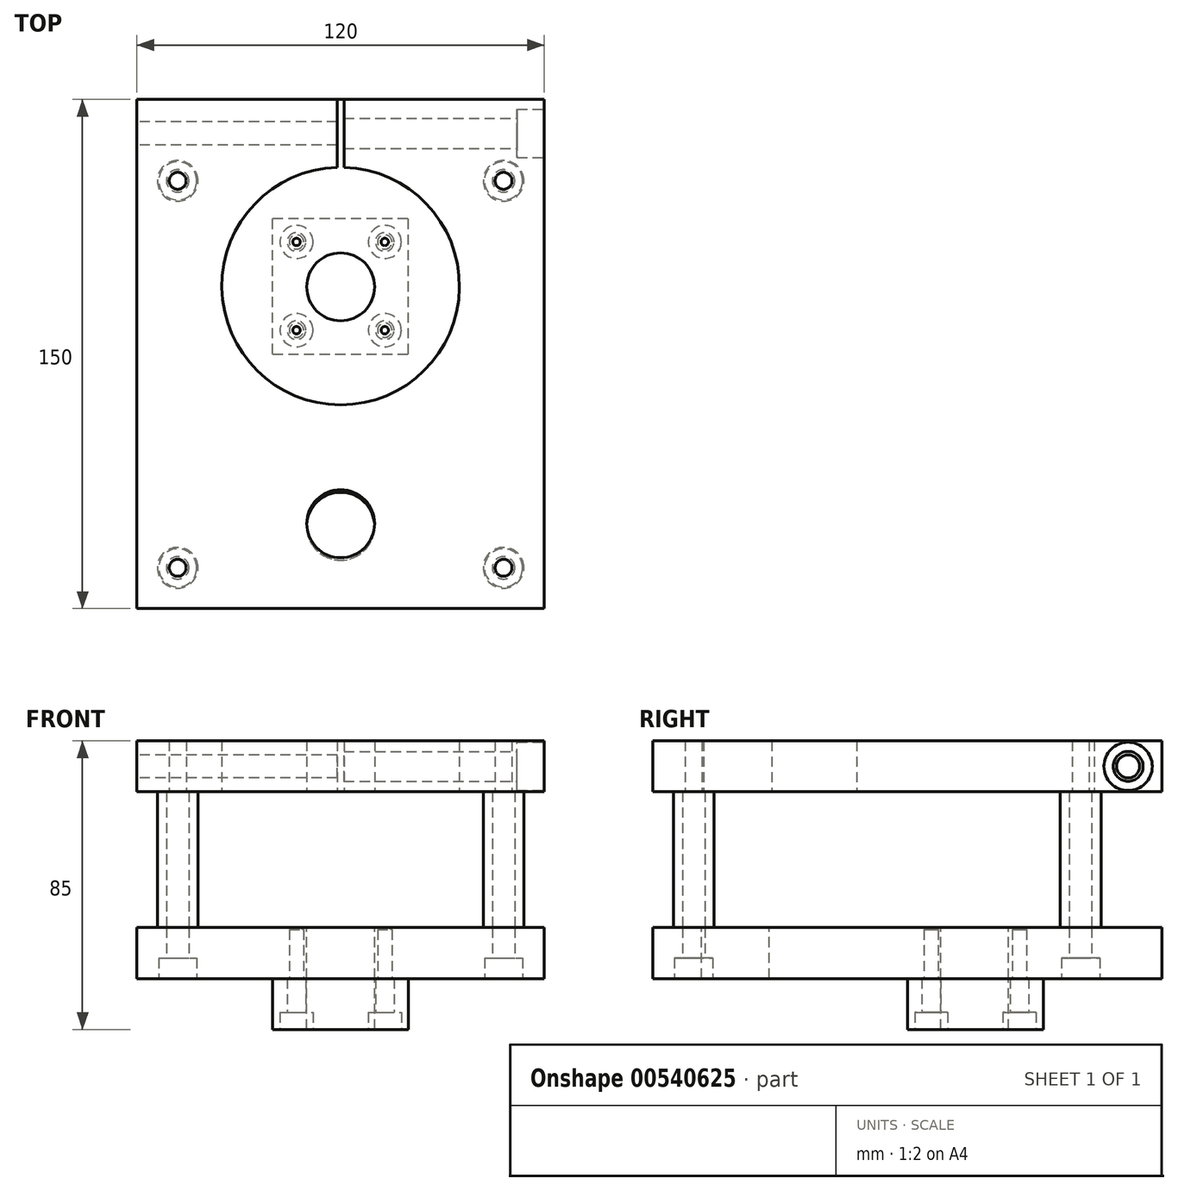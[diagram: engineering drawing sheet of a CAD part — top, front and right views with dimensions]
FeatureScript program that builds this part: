
annotation { "Feature Type Name" : "Feature", "Feature Type Description" : "" }
export const myFeature = defineFeature(function(context is Context, id is Id, definition is map)
    precondition{}
    {
        {
            var Q0;
            Q0=qCreatedBy(makeId("Top.planeOp"),FACE);
            var sketch = newSketch(context, id + "F0", { "sketchPlane" : qUnion([Q0])});
            skLineSegment(sketch, "E0.bottom", {"start": v(-60, 75) * mm, "end": v(-1, 75) * mm});
            skLineSegment(sketch, "E0.top", {"start": v(-60, -75) * mm, "end": v(60, -75) * mm});
            skLineSegment(sketch, "E0.left", {"start": v(-60, 75) * mm, "end": v(-60, -75) * mm});
            skLineSegment(sketch, "E0.right", {"start": v(60, 75) * mm, "end": v(60, -75) * mm});
            skLineSegment(sketch, "E1", {"start": v(0, 75) * mm, "end": v(0, -75) * mm, "construction": true});
            skLineSegment(sketch, "E2", {"start": v(-60, 0) * mm, "end": v(60, 0) * mm, "construction": true});
            skArc(sketch, "E3", {"start": v(-1, 54.99) * mm, "mid": v(0, -15) * mm, "end": v(1, 54.99) * mm});
            skLineSegment(sketch, "E4.0", {"start": v(-1, 75) * mm, "end": v(-1, 54.99) * mm});
            skLineSegment(sketch, "E5.0", {"start": v(1, 75) * mm, "end": v(1, 54.99) * mm});
            skLineSegment(sketch, "E6.trimOffspring", {"start": v(1, 75) * mm, "end": v(60, 75) * mm});
            skLineSegment(sketch, "E7", {"start": v(60, 51) * mm, "end": v(-60, 51) * mm, "construction": true});
            skCircle(sketch, "E8", {"center": v(0, -50) * mm, "radius": 10 * mm});
            skLineSegment(sketch, "E9.0", {"start": v(48, 75) * mm, "end": v(48, -75) * mm, "construction": true});
            skLineSegment(sketch, "E10.0", {"start": v(-48, 75) * mm, "end": v(-48, -75) * mm, "construction": true});
            skLineSegment(sketch, "E11.0", {"start": v(-60, -63) * mm, "end": v(60, -63) * mm, "construction": true});
            skPoint(sketch, "E12", {"position": v(-48, 51) * mm});
            skPoint(sketch, "E13", {"position": v(48, 51) * mm});
            skPoint(sketch, "E14", {"position": v(48, -63) * mm});
            skPoint(sketch, "E15", {"position": v(-48, -63) * mm});
            skCircle(sketch, "E16", {"center": v(-48, 51) * mm, "radius": 6 * mm});
            skCircle(sketch, "E17", {"center": v(48, 51) * mm, "radius": 6 * mm});
            skCircle(sketch, "E18", {"center": v(48, -63) * mm, "radius": 6 * mm});
            skCircle(sketch, "E19", {"center": v(-48, -63) * mm, "radius": 6 * mm});
            skSolve(sketch);
        }
        {
            var Q0;
            Q0=makeQuery(id+"F0.imprint","IMPRINT",FACE,{"disambiguationData":[TD([[makeQuery(id+"F0.imprint","IMPRINT",EDGE,{"derivedFrom":sQuery(id+"F0.wireOp",EDGE,"E0.bottom")}),-1.0]])]});
            var Q1;
            Q1=makeQuery(id+"F0.imprint","IMPRINT",FACE,{"disambiguationData":[TD([[makeQuery(id+"F0.imprint","IMPRINT",EDGE,{"derivedFrom":sQuery(id+"F0.wireOp",EDGE,"E19")}),1.0]])]});
            var Q2;
            Q2=makeQuery(id+"F0.imprint","IMPRINT",FACE,{"disambiguationData":[TD([[makeQuery(id+"F0.imprint","IMPRINT",EDGE,{"derivedFrom":sQuery(id+"F0.wireOp",EDGE,"E18")}),1.0]])]});
            var Q3;
            Q3=makeQuery(id+"F0.imprint","IMPRINT",FACE,{"disambiguationData":[TD([[makeQuery(id+"F0.imprint","IMPRINT",EDGE,{"derivedFrom":sQuery(id+"F0.wireOp",EDGE,"E17")}),1.0]])]});
            var Q4;
            Q4=makeQuery(id+"F0.imprint","IMPRINT",FACE,{"disambiguationData":[TD([[makeQuery(id+"F0.imprint","IMPRINT",EDGE,{"derivedFrom":sQuery(id+"F0.wireOp",EDGE,"E16")}),1.0]])]});
            extrude(context, id + "F1", {"entities" : qUnion([Q0, Q1, Q2, Q3, Q4]), "depth" : 15 * mm, "offsetDistance" : 25 * mm});
        }
        {
            var Q0;
            Q0=makeQuery(id+"F0.imprint","IMPRINT",FACE,{"disambiguationData":[TD([[makeQuery(id+"F0.imprint","IMPRINT",EDGE,{"derivedFrom":sQuery(id+"F0.wireOp",EDGE,"E17")}),1.0]])]});
            var Q1;
            Q1=makeQuery(id+"F0.imprint","IMPRINT",FACE,{"disambiguationData":[TD([[makeQuery(id+"F0.imprint","IMPRINT",EDGE,{"derivedFrom":sQuery(id+"F0.wireOp",EDGE,"E16")}),1.0]])]});
            var Q2;
            Q2=makeQuery(id+"F0.imprint","IMPRINT",FACE,{"disambiguationData":[TD([[makeQuery(id+"F0.imprint","IMPRINT",EDGE,{"derivedFrom":sQuery(id+"F0.wireOp",EDGE,"E19")}),1.0]])]});
            var Q3;
            Q3=makeQuery(id+"F0.imprint","IMPRINT",FACE,{"disambiguationData":[TD([[makeQuery(id+"F0.imprint","IMPRINT",EDGE,{"derivedFrom":sQuery(id+"F0.wireOp",EDGE,"E18")}),1.0]])]});
            extrude(context, id + "F2", {"entities" : qUnion([Q0, Q1, Q2, Q3]), "oppositeDirection" : true, "depth" : 40 * mm, "offsetDistance" : 25 * mm});
        }
        {
            var Q0;
            Q0=makeQuery(id+"F2.opExtrude","CAP_FACE",FACE,{"disambiguationData":[OSD([sQuery(id+"F0.wireOp",EDGE,"E19")])],"isStart":false});
            var sketch = newSketch(context, id + "F3", { "sketchPlane" : qUnion([Q0])});
            skLineSegment(sketch, "E20.0", {"start": v(-60, -75) * mm, "end": v(-60, 75) * mm});
            skLineSegment(sketch, "E21.0", {"start": v(-60, 75) * mm, "end": v(60, 75) * mm});
            skLineSegment(sketch, "E22.0", {"start": v(60, -75) * mm, "end": v(60, 75) * mm});
            skLineSegment(sketch, "E23", {"start": v(-60, -75) * mm, "end": v(60, -75) * mm});
            skCircle(sketch, "E24", {"center": v(0, 50.75) * mm, "radius": 10 * mm});
            skCircle(sketch, "E25", {"center": v(0, -19.77) * mm, "radius": 10 * mm});
            skSolve(sketch);
        }
        {
            var Q0;
            Q0=makeQuery(id+"F3.imprint","IMPRINT",FACE,{"disambiguationData":[TD([[makeQuery(id+"F3.imprint","IMPRINT",EDGE,{"derivedFrom":sQuery(id+"F3.wireOp",EDGE,"E20.0")}),-1.0]])]});
            var Q1;
            Q1=makeQuery(id+"F3.imprint","IMPRINT",FACE,{"disambiguationData":[TD([[makeQuery(id+"F3.imprint","IMPRINT",EDGE,{"derivedFrom":makeQuery(id+"F2.opExtrude","CAP_EDGE",EDGE,{"disambiguationData":[OSD([sQuery(id+"F0.wireOp",EDGE,"E19")])],"isStart":false})}),-1.0]])]});
            extrude(context, id + "F4", {"entities" : qUnion([Q0, Q1]), "depth" : 15 * mm, "offsetDistance" : 25 * mm});
        }
        {
            var Q0;
            Q0=makeQuery(id+"F4.opExtrude","CAP_FACE",FACE,{"disambiguationData":[OSD([sQuery(id+"F3.wireOp",EDGE,"E20.0"),sQuery(id+"F3.wireOp",EDGE,"E21.0"),sQuery(id+"F3.wireOp",EDGE,"E22.0"),sQuery(id+"F3.wireOp",EDGE,"E23"),sQuery(id+"F3.wireOp",EDGE,"E24"),sQuery(id+"F3.wireOp",EDGE,"E25")])],"isStart":false});
            var sketch = newSketch(context, id + "F5", { "sketchPlane" : qUnion([Q0])});
            skPoint(sketch, "E26.0", {"position": v(48, -51) * mm});
            skPoint(sketch, "E27.0", {"position": v(-48, -51) * mm});
            skPoint(sketch, "E28.0", {"position": v(48, 63) * mm});
            skPoint(sketch, "E29.0", {"position": v(-48, 63) * mm});
            skLineSegment(sketch, "E30.bottom", {"start": v(-20, 0) * mm, "end": v(20, 0) * mm});
            skLineSegment(sketch, "E30.top", {"start": v(-20, -40) * mm, "end": v(20, -40) * mm});
            skLineSegment(sketch, "E30.left", {"start": v(-20, 0) * mm, "end": v(-20, -40) * mm});
            skLineSegment(sketch, "E30.right", {"start": v(20, 0) * mm, "end": v(20, -40) * mm});
            skLineSegment(sketch, "E31", {"start": v(-20, -20) * mm, "end": v(20, -20) * mm, "construction": true});
            skLineSegment(sketch, "E32", {"start": v(0, 0) * mm, "end": v(0, -40) * mm, "construction": true});
            skSolve(sketch);
        }
        {
            var Q0;
            Q0=sQuery(id+"F5.wireOp",VERTEX,"E29.0");
            var Q1;
            Q1=sQuery(id+"F5.wireOp",VERTEX,"E28.0");
            var Q2;
            Q2=sQuery(id+"F5.wireOp",VERTEX,"E26.0");
            var Q3;
            Q3=sQuery(id+"F5.wireOp",VERTEX,"E27.0");
            var Q4;
            Q4=makeQuery(id+"F1.opExtrude","SWEPT_BODY",BODY,{"disambiguationData":[OSD([sQuery(id+"F0.wireOp",EDGE,"E0.bottom"),sQuery(id+"F0.wireOp",EDGE,"E0.top"),sQuery(id+"F0.wireOp",EDGE,"E0.left"),sQuery(id+"F0.wireOp",EDGE,"E0.right"),sQuery(id+"F0.wireOp",EDGE,"E3"),sQuery(id+"F0.wireOp",EDGE,"E4.0"),sQuery(id+"F0.wireOp",EDGE,"E5.0"),sQuery(id+"F0.wireOp",EDGE,"E6.trimOffspring"),sQuery(id+"F0.wireOp",EDGE,"E8")])]});
            var Q5;
            Q5=makeQuery(id+"F2.opExtrude","SWEPT_BODY",BODY,{"disambiguationData":[OSD([sQuery(id+"F0.wireOp",EDGE,"E19")])]});
            var Q6;
            Q6=makeQuery(id+"F4.opExtrude","SWEPT_BODY",BODY,{"disambiguationData":[OSD([sQuery(id+"F3.wireOp",EDGE,"E20.0"),sQuery(id+"F3.wireOp",EDGE,"E21.0"),sQuery(id+"F3.wireOp",EDGE,"E22.0"),sQuery(id+"F3.wireOp",EDGE,"E23"),sQuery(id+"F3.wireOp",EDGE,"E24"),sQuery(id+"F3.wireOp",EDGE,"E25")])]});
            var Q7;
            Q7=makeQuery(id+"F2.opExtrude","SWEPT_BODY",BODY,{"disambiguationData":[OSD([sQuery(id+"F0.wireOp",EDGE,"E18")])]});
            var Q8;
            Q8=makeQuery(id+"F2.opExtrude","SWEPT_BODY",BODY,{"disambiguationData":[OSD([sQuery(id+"F0.wireOp",EDGE,"E17")])]});
            var Q9;
            Q9=makeQuery(id+"F2.opExtrude","SWEPT_BODY",BODY,{"disambiguationData":[OSD([sQuery(id+"F0.wireOp",EDGE,"E16")])]});
            hole(context, id + "F6", {"style" : HoleStyle.C_BORE, "endStyle" : HoleEndStyle.BLIND_IN_LAST, "standardTappedOrClearance" : lookupTablePath({ "fit" : "Normal", "standard" : "ISO", "engagement" : "75%", "pitch" : "1 mm", "size" : "M6", "type" : "Clearance & tapped" }), "standardBlindInLast" : lookupTablePath({ "standard" : "ISO", "fit" : "Standard", "engagement" : "75%", "pitch" : "1 mm", "size" : "M6", "type" : "Clearance & tapped" }), "holeDiameter" : 6.6 * mm, "cBoreDiameter" : 11.25 * mm, "cBoreDepth" : 6 * mm, "tapDrillDiameter" : 5 * mm, "showTappedDepth" : true, "holeDepth" : 15 * mm, "isTappedThrough" : true, "tappedDepth" : 12 * mm, "tapClearance" : 3, "locations" : qUnion([Q0, Q1, Q2, Q3]), "scope" : qUnion([Q4, Q5, Q6, Q7, Q8, Q9]), "majorDiameter" : 6 * mm});
        }
        {
            var Q0;
            Q0=makeQuery(id+"F5.imprint","IMPRINT",FACE,{"disambiguationData":[TD([[makeQuery(id+"F5.imprint","IMPRINT",EDGE,{"derivedFrom":sQuery(id+"F5.wireOp",EDGE,"E30.bottom")}),-1.0]])]});
            extrude(context, id + "F7", {"entities" : qUnion([Q0]), "depth" : 15 * mm, "offsetDistance" : 25 * mm});
        }
        {
            var Q0;
            Q0=makeQuery(id+"F7.opExtrude","CAP_FACE",FACE,{"disambiguationData":[OSD([sQuery(id+"F3.wireOp",EDGE,"E25"),sQuery(id+"F5.wireOp",EDGE,"E30.bottom"),sQuery(id+"F5.wireOp",EDGE,"E30.top"),sQuery(id+"F5.wireOp",EDGE,"E30.left"),sQuery(id+"F5.wireOp",EDGE,"E30.right")])],"isStart":false});
            var sketch = newSketch(context, id + "F8", { "sketchPlane" : qUnion([Q0])});
            skLineSegment(sketch, "E33.0", {"start": v(-13, -7) * mm, "end": v(-13, -33) * mm, "construction": true});
            skLineSegment(sketch, "E33.1", {"start": v(-13, -7) * mm, "end": v(13, -7) * mm, "construction": true});
            skLineSegment(sketch, "E33.2", {"start": v(13, -7) * mm, "end": v(13, -33) * mm, "construction": true});
            skLineSegment(sketch, "E33.3", {"start": v(-13, -33) * mm, "end": v(13, -33) * mm, "construction": true});
            skPoint(sketch, "E34", {"position": v(-13, -7) * mm});
            skPoint(sketch, "E35", {"position": v(13, -7) * mm});
            skPoint(sketch, "E36", {"position": v(13, -33) * mm});
            skPoint(sketch, "E37", {"position": v(-13, -33) * mm});
            skSolve(sketch);
        }
        {
            var Q0;
            Q0=sQuery(id+"F8.wireOp",VERTEX,"E33.0.start");
            var Q1;
            Q1=sQuery(id+"F8.wireOp",VERTEX,"E33.2.start");
            var Q2;
            Q2=sQuery(id+"F8.wireOp",VERTEX,"E33.3.end");
            var Q3;
            Q3=sQuery(id+"F8.wireOp",VERTEX,"E33.3.start");
            var Q4;
            Q4=makeQuery(id+"F7.opExtrude","SWEPT_BODY",BODY,{"disambiguationData":[OSD([sQuery(id+"F3.wireOp",EDGE,"E25"),sQuery(id+"F5.wireOp",EDGE,"E30.bottom"),sQuery(id+"F5.wireOp",EDGE,"E30.top"),sQuery(id+"F5.wireOp",EDGE,"E30.left"),sQuery(id+"F5.wireOp",EDGE,"E30.right")])]});
            var Q5;
            Q5=makeQuery(id+"F4.opExtrude","SWEPT_BODY",BODY,{"disambiguationData":[OSD([sQuery(id+"F3.wireOp",EDGE,"E20.0"),sQuery(id+"F3.wireOp",EDGE,"E21.0"),sQuery(id+"F3.wireOp",EDGE,"E22.0"),sQuery(id+"F3.wireOp",EDGE,"E23"),sQuery(id+"F3.wireOp",EDGE,"E24"),sQuery(id+"F3.wireOp",EDGE,"E25")])]});
            hole(context, id + "F9", {"style" : HoleStyle.C_BORE, "endStyle" : HoleEndStyle.BLIND_IN_LAST, "standardTappedOrClearance" : lookupTablePath({ "fit" : "Normal", "standard" : "ISO", "engagement" : "75%", "pitch" : "0.8 mm", "size" : "M5", "type" : "Clearance & tapped" }), "standardBlindInLast" : lookupTablePath({ "standard" : "ISO", "fit" : "Standard", "engagement" : "75%", "pitch" : "0.8 mm", "size" : "M5", "type" : "Clearance & tapped" }), "holeDiameter" : 5.5 * mm, "cBoreDiameter" : 9.75 * mm, "cBoreDepth" : 5 * mm, "tapDrillDiameter" : 4.2 * mm, "showTappedDepth" : true, "holeDepth" : 14.4 * mm, "isTappedThrough" : true, "tappedDepth" : 12 * mm, "tapClearance" : 3, "locations" : qUnion([Q0, Q1, Q2, Q3]), "scope" : qUnion([Q4, Q5]), "majorDiameter" : 5 * mm});
        }
        {
            var Q0;
            Q0=makeQuery(id+"F1.opExtrude","SWEPT_FACE",FACE,{"disambiguationData":[OSD([sQuery(id+"F0.wireOp",EDGE,"E0.right")])]});
            var sketch = newSketch(context, id + "F10", { "sketchPlane" : qUnion([Q0])});
            skLineSegment(sketch, "E38", {"start": v(75, 7.5) * mm, "end": v(-75, 7.5) * mm, "construction": true});
            skPoint(sketch, "E39", {"position": v(65, 7.5) * mm});
            skSolve(sketch);
        }
        {
            var Q0;
            Q0=sQuery(id+"F10.wireOp",VERTEX,"E39");
            var Q1;
            Q1=makeQuery(id+"F1.opExtrude","SWEPT_BODY",BODY,{"disambiguationData":[OSD([sQuery(id+"F0.wireOp",EDGE,"E0.bottom"),sQuery(id+"F0.wireOp",EDGE,"E0.top"),sQuery(id+"F0.wireOp",EDGE,"E0.left"),sQuery(id+"F0.wireOp",EDGE,"E0.right"),sQuery(id+"F0.wireOp",EDGE,"E3"),sQuery(id+"F0.wireOp",EDGE,"E4.0"),sQuery(id+"F0.wireOp",EDGE,"E5.0"),sQuery(id+"F0.wireOp",EDGE,"E6.trimOffspring"),sQuery(id+"F0.wireOp",EDGE,"E8")])]});
            hole(context, id + "F11", {"style" : HoleStyle.C_BORE, "endStyle" : HoleEndStyle.BLIND, "standardTappedOrClearance" : lookupTablePath({ "standard" : "ISO", "fit" : "Normal", "size" : "M8", "type" : "Clearance" }), "standardBlindInLast" : lookupTablePath({ "fit" : "Standard", "standard" : "ISO", "size" : "M8", "type" : "Clearance" }), "holeDiameter" : 8.8 * mm, "cBoreDiameter" : 14.25 * mm, "cBoreDepth" : 8 * mm, "holeDepth" : 60 * mm, "isTappedThrough" : true, "tappedDepth" : 12 * mm, "tapClearance" : 3, "locations" : qUnion([Q0]), "scope" : qUnion([Q1])});
        }
        {
            var Q0;
            Q0=makeQuery(id+"F1.opExtrude","SWEPT_FACE",FACE,{"disambiguationData":[OSD([sQuery(id+"F0.wireOp",EDGE,"E0.left")])]});
            var sketch = newSketch(context, id + "F12", { "sketchPlane" : qUnion([Q0])});
            skPoint(sketch, "E40.0", {"position": v(-65, 7.5) * mm});
            skSolve(sketch);
        }
        {
            var Q0;
            Q0=sQuery(id+"F12.wireOp",VERTEX,"E40.0");
            var Q1;
            Q1=makeQuery(id+"F1.opExtrude","SWEPT_BODY",BODY,{"disambiguationData":[OSD([sQuery(id+"F0.wireOp",EDGE,"E0.bottom"),sQuery(id+"F0.wireOp",EDGE,"E0.top"),sQuery(id+"F0.wireOp",EDGE,"E0.left"),sQuery(id+"F0.wireOp",EDGE,"E0.right"),sQuery(id+"F0.wireOp",EDGE,"E3"),sQuery(id+"F0.wireOp",EDGE,"E4.0"),sQuery(id+"F0.wireOp",EDGE,"E5.0"),sQuery(id+"F0.wireOp",EDGE,"E6.trimOffspring"),sQuery(id+"F0.wireOp",EDGE,"E8")])]});
            hole(context, id + "F13", {"style" : HoleStyle.SIMPLE, "endStyle" : HoleEndStyle.BLIND, "standardTappedOrClearance" : lookupTablePath({ "standard" : "ISO", "engagement" : "75%", "pitch" : "1.25 mm", "size" : "M8", "type" : "Tapped" }), "standardBlindInLast" : lookupTablePath({ "standard" : "ISO", "engagement" : "75%", "pitch" : "1.25 mm", "size" : "M8", "type" : "Tapped" }), "holeDiameter" : 6.8 * mm, "showTappedDepth" : true, "holeDepth" : 60 * mm, "isTappedThrough" : true, "tappedDepth" : 56.25 * mm, "tapClearance" : 3, "locations" : qUnion([Q0]), "scope" : qUnion([Q1]), "majorDiameter" : 8 * mm});
        }
    });
